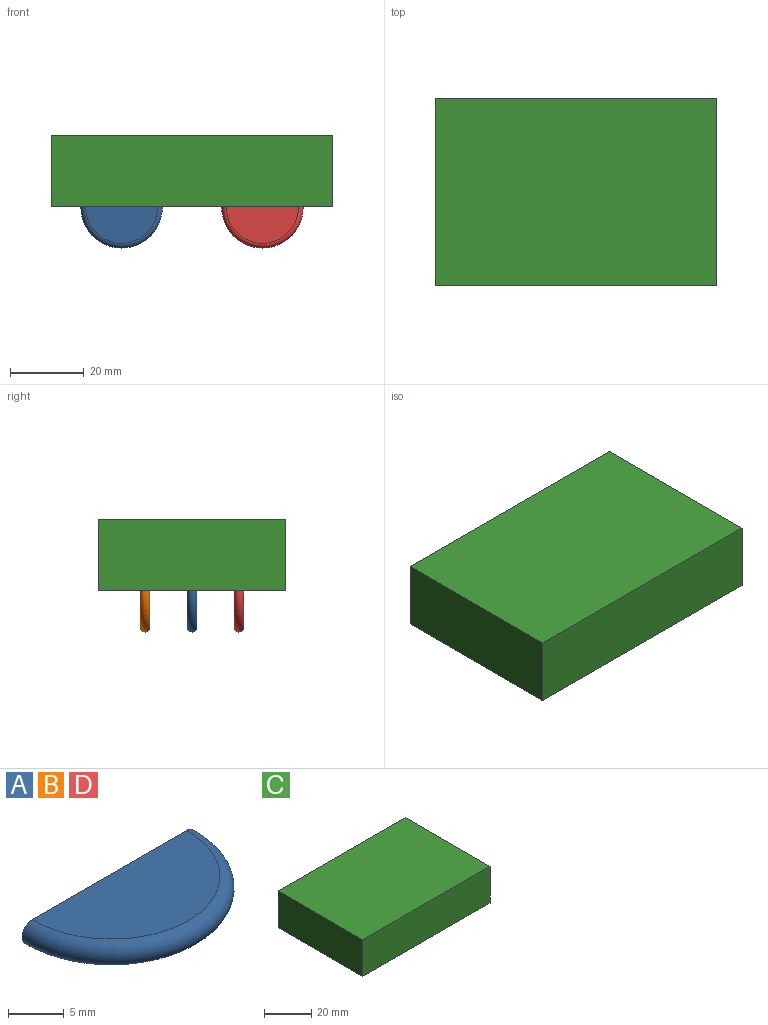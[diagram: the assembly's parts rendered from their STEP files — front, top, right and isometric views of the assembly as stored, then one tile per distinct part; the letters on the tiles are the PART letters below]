
ASSEMBLY  parts=4 mates=3
PART A: 4 faces, bbox 23.8x12.2x2.6 mm
  f0: plane 22.03x2.55mm, normal (0,1,0), area 54.5mm2, adj f1,f2,f3
  f1: plane 19.48x9.98mm, normal (0,0,1), area 153.8mm2, adj f0,f3
  f2: plane 19.48x9.98mm, normal (0,0,-1), area 153.8mm2, adj f0,f3
  f3: torus R=9.74mm, axis (0,0,1), area 134.2mm2, adj f0,f1,f2
PART B: same geometry as A
PART C: 6 faces, bbox 76.2x50.8x19.1 mm
  f0: plane 76.2x19.05mm, normal (0,1,0), area 1451.6mm2, adj f1,f3,f4,f5
  f1: plane 50.8x19.05mm, normal (-1,0,0), area 967.7mm2, adj f0,f2,f4,f5
  f2: plane 76.2x19.05mm, normal (0,-1,0), area 1451.6mm2, adj f1,f3,f4,f5
  f3: plane 50.8x19.05mm, normal (1,0,0), area 967.7mm2, adj f0,f2,f4,f5
  f4: plane 76.2x50.8mm, normal (0,0,1), area 3871mm2, adj f0,f1,f2,f3
  f5: plane 76.2x50.8mm, normal (0,0,-1), area 3871mm2, adj f0,f1,f2,f3
PART D: same geometry as A
PLACE A rot(axis=(1,0,0),90deg) t=(-13.89,52.82,5.76)mm
PLACE B rot(axis=(1,0,0),90deg) t=(24.21,65.52,5.76)mm
PLACE C t=(-0.2,26.15,5.76)mm
PLACE D rot(axis=(1,0,0),90deg) t=(24.21,40.12,5.76)mm
MATE fastened D.f0 <-> C.f5  axis (0,0,1) through (13.2,38.85,5.76)mm
MATE fastened A.f0 <-> C.f5  axis (0,0,1) through (-24.9,51.55,5.76)mm
MATE fastened B.f0 <-> C.f5  axis (0,0,1) through (13.2,64.25,5.76)mm
